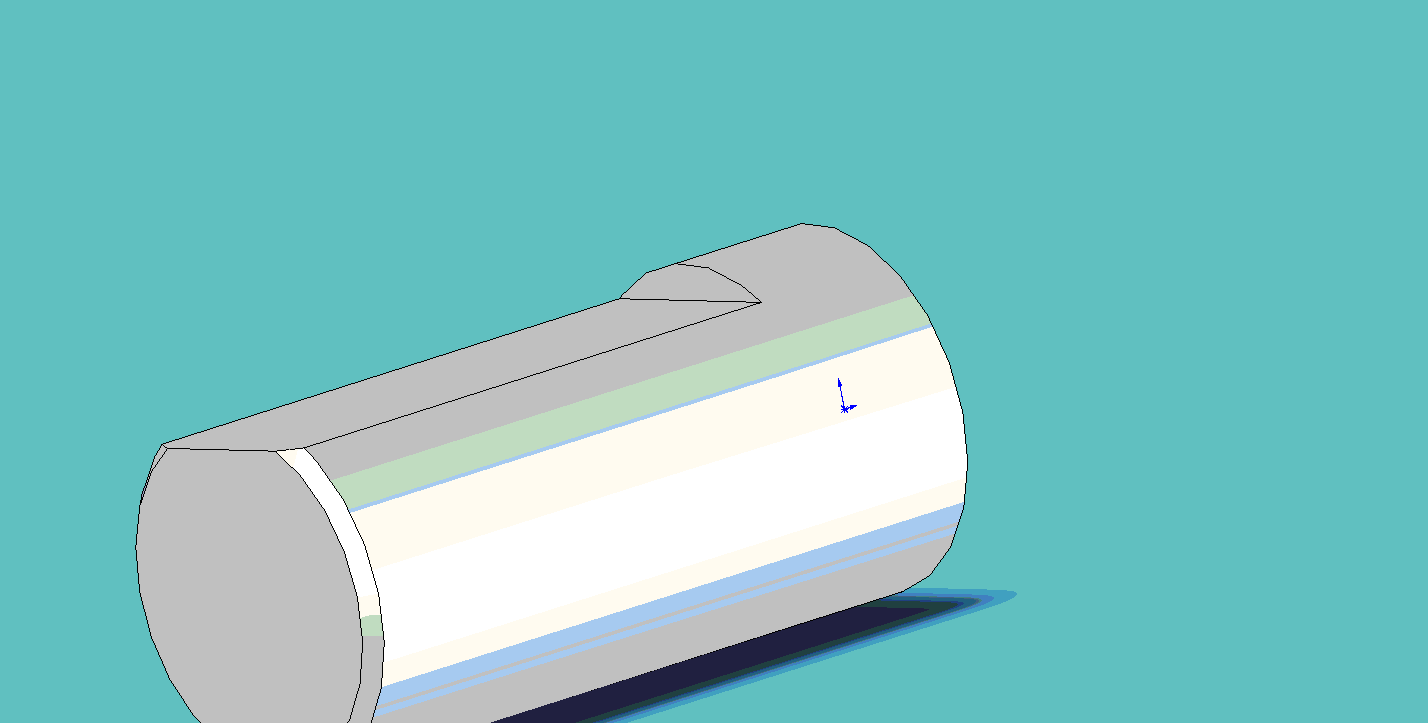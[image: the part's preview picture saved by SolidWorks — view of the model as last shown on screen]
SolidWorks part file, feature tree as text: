
SOLIDWORKS PART (.sldprt)
format: sldprt  version: not decoded by parser v0  size: 108,032 bytes
history: native  units: mm
features: plane x3, sketch x2, material x1, revolve x1, cut_extrude x1, chamfer x1 (+12 scaffold rows collapsed)
feature tree (21):
  scaffold x12  (default folders/planes/origin — collapsed)
  material  "Matériau <non spécifié>"
  plane  "Plan de face"
  plane  "Plan de dessus"
  plane  "Plan de droite"
  sketch  "Esquisse1"  dims[D1=5.0mm D2=10.15mm]
  revolve  "Révolution1"  Angle=360deg
  sketch  "Esquisse2"  dims[D1=4.5mm]
  cut_extrude  "Enlèv. mat.-Extru.1"  Depth=8mm
  chamfer  "Chanfrein1"  Distance=0.2mm Angle=45deg
decode coverage: 5 of 5 modeling features carry decoded parameters
note: suppression state not decoded; provenance and decode notes live in map.json
